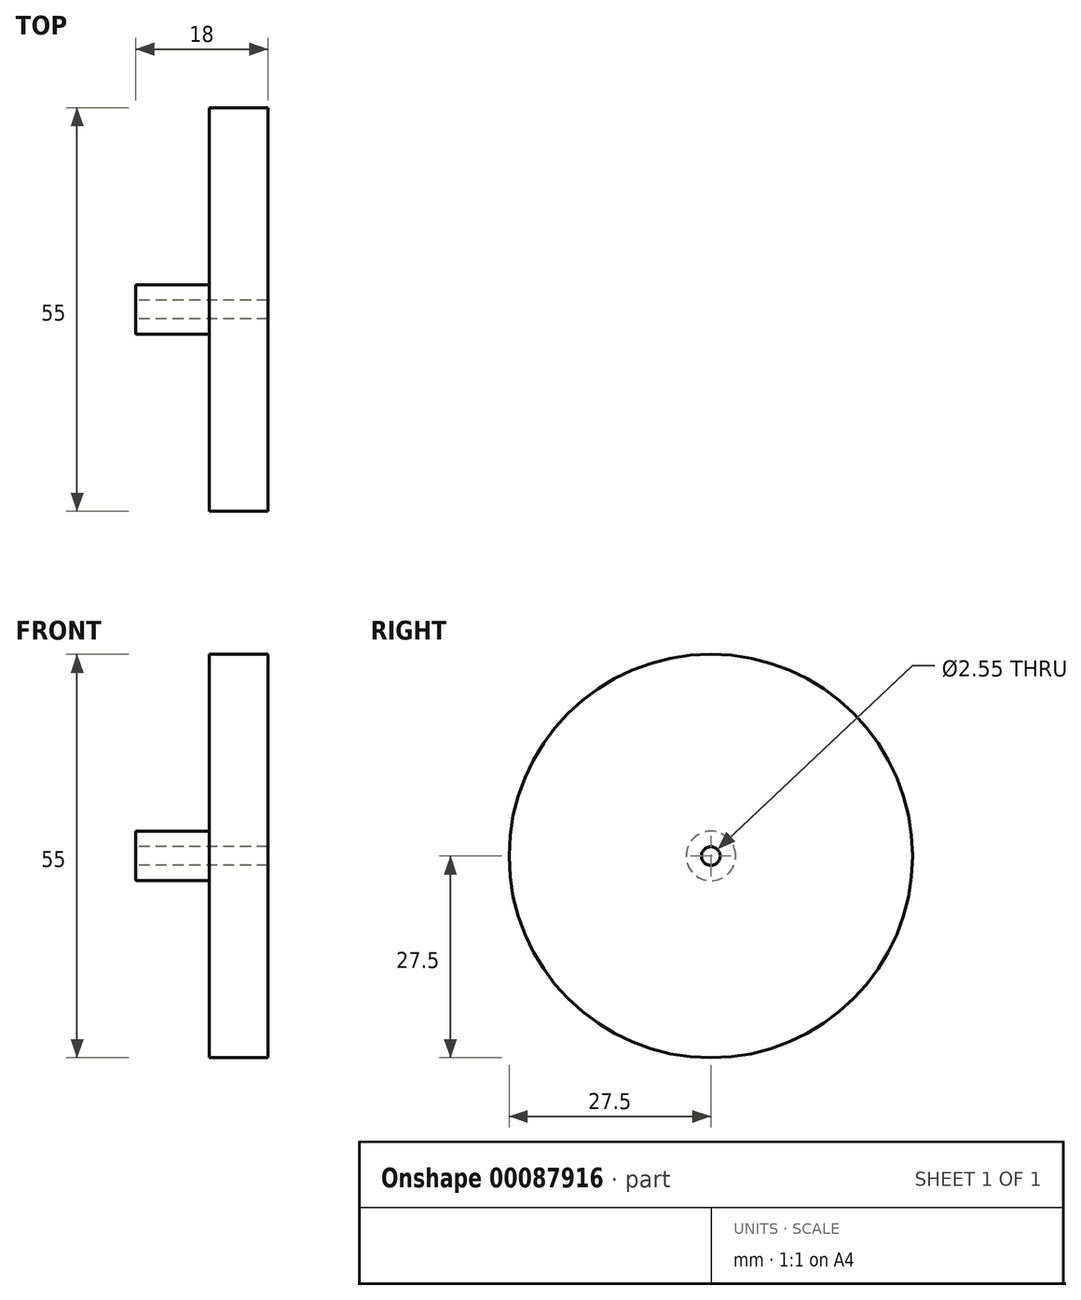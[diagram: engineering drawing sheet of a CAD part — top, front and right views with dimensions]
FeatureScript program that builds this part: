
annotation { "Feature Type Name" : "Feature", "Feature Type Description" : "" }
export const myFeature = defineFeature(function(context is Context, id is Id, definition is map)
    precondition{}
    {
        {
            var Q0;
            Q0=qCreatedBy(makeId("Right.planeOp"),FACE);
            var sketch = newSketch(context, id + "F0", { "sketchPlane" : qUnion([Q0])});
            skCircle(sketch, "E0", {"center": v(0, 0) * mm, "radius": 3.38 * mm});
            skSolve(sketch);
        }
        {
            var Q0;
            Q0=qSketchRegion(id+"F0",true);
            extrude(context, id + "F1", {"entities" : qUnion([Q0]), "depth" : 10 * mm});
        }
        {
            var Q0;
            Q0=makeQuery(id+"F1.opExtrude","CAP_FACE",FACE,{"disambiguationData":[OSD([sQuery(id+"F0.wireOp",EDGE,"E0")])],"isStart":false});
            var sketch = newSketch(context, id + "F2", { "sketchPlane" : qUnion([Q0])});
            skCircle(sketch, "E1", {"center": v(0, 0) * mm, "radius": 27.5 * mm});
            skSolve(sketch);
        }
        {
            var Q0;
            Q0=makeQuery(id+"F2.imprint","IMPRINT",FACE,{"disambiguationData":[TD([[makeQuery(id+"F2.imprint","IMPRINT",EDGE,{"derivedFrom":sQuery(id+"F2.wireOp",EDGE,"E1")}),1.0]])]});
            var Q1;
            Q1=makeQuery(id+"F2.imprint","IMPRINT",FACE,{"disambiguationData":[TD([[makeQuery(id+"F2.imprint","IMPRINT",EDGE,{"derivedFrom":makeQuery(id+"F1.opExtrude","CAP_EDGE",EDGE,{"disambiguationData":[OSD([sQuery(id+"F0.wireOp",EDGE,"E0")])],"isStart":false})}),1.0]])]});
            extrude(context, id + "F3", {"entities" : qUnion([Q0, Q1]), "operationType" : NewBodyOperationType.ADD, "depth" : 8 * mm});
        }
        {
            var Q0;
            Q0=makeQuery(id+"F1.opExtrude","CAP_FACE",FACE,{"disambiguationData":[OSD([sQuery(id+"F0.wireOp",EDGE,"E0")])],"isStart":true});
            var sketch = newSketch(context, id + "F4", { "sketchPlane" : qUnion([Q0])});
            skCircle(sketch, "E2", {"center": v(0, 0) * mm, "radius": 1.27 * mm});
            skSolve(sketch);
        }
        {
            var Q0;
            Q0=qSketchRegion(id+"F4",true);
            extrude(context, id + "F5", {"entities" : qUnion([Q0]), "operationType" : NewBodyOperationType.REMOVE, "oppositeDirection" : true, "depth" : 25.4 * mm});
        }
    });
